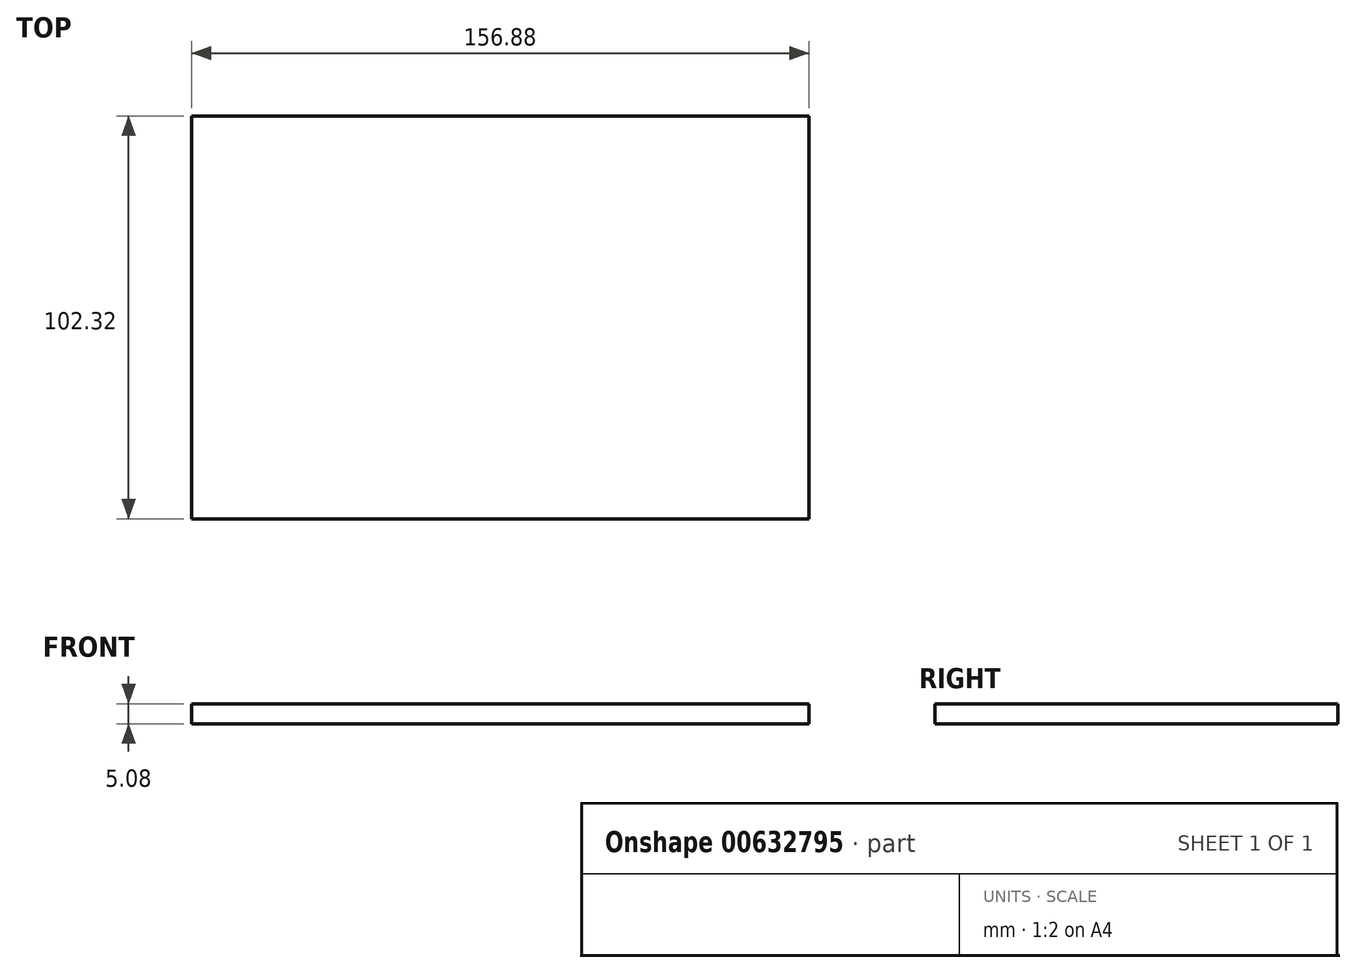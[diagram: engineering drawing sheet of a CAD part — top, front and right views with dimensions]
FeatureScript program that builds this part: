
annotation { "Feature Type Name" : "Feature", "Feature Type Description" : "" }
export const myFeature = defineFeature(function(context is Context, id is Id, definition is map)
    precondition{}
    {
        {
            var Q0;
            Q0=qCreatedBy(makeId("Top.planeOp"),FACE);
            var sketch = newSketch(context, id + "F0", { "sketchPlane" : qUnion([Q0])});
            skLineSegment(sketch, "E0.bottom", {"start": v(78.44, 51.16) * mm, "end": v(-78.44, 51.16) * mm});
            skLineSegment(sketch, "E0.top", {"start": v(78.44, -51.16) * mm, "end": v(-78.44, -51.16) * mm});
            skLineSegment(sketch, "E0.left", {"start": v(78.44, 51.16) * mm, "end": v(78.44, -51.16) * mm});
            skLineSegment(sketch, "E0.right", {"start": v(-78.44, 51.16) * mm, "end": v(-78.44, -51.16) * mm});
            skPoint(sketch, "E0.middle", {"position": v(0, 0) * mm});
            skSolve(sketch);
        }
        {
            var Q0;
            Q0=makeQuery(id+"F0.imprint","IMPRINT",FACE,{"disambiguationData":[TD([[makeQuery(id+"F0.imprint","IMPRINT",EDGE,{"derivedFrom":sQuery(id+"F0.wireOp",EDGE,"E0.bottom")}),1.0]])]});
            extrude(context, id + "F1", {"entities" : qUnion([Q0]), "depth" : 5.08 * mm, "offsetDistance" : 25.4 * mm});
        }
    });
